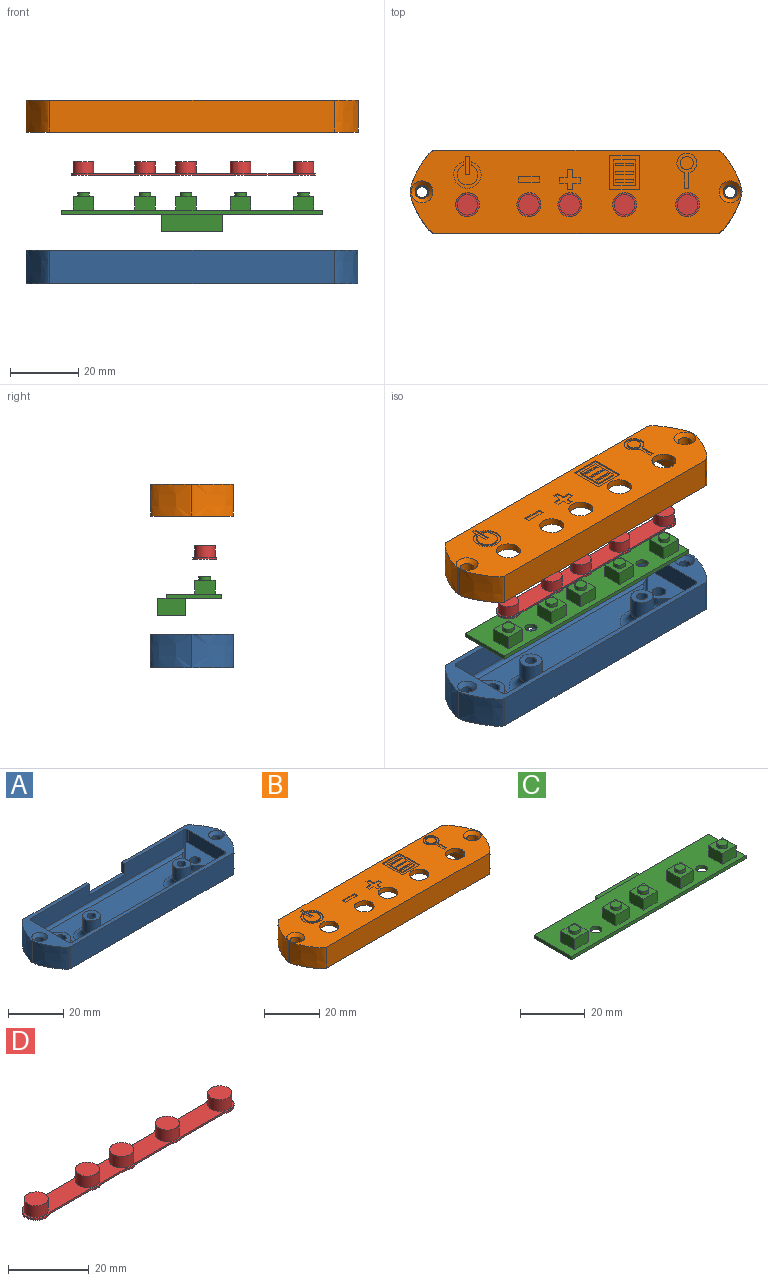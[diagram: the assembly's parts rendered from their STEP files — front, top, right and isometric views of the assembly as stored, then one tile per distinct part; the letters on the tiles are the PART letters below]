
ASSEMBLY  parts=4 mates=3
PART A: 54 faces, bbox 97.2x24.2x9.7 mm
  f0: cylinder r=2mm len=4mm, axis (0,0,1), area 50.3mm2, adj f12,f35
  f1: cylinder r=2mm len=4mm, axis (0,0,1), area 50.3mm2, adj f12,f33
  f2: plane 97.15x24.2mm, normal (0,0,1), area 457.5mm2, adj f3,f4,f5,f6,f7,f8,f11,f16
  f3: plane 77.75x7.8mm, normal (0,-1,0), area 520.1mm2, adj f2,f21,f22,f23,f37,f39,f40
  f4: extruded ~12.1x9.7mm, area 139.3mm2, adj f2,f5,f11,f12
  f5: plane 83.15x9.7mm, normal (0,1,0), area 720.2mm2, adj f2,f4,f6,f12,f21,f22,f23
  f6: extruded ~12.1x9.7mm, area 139.3mm2, adj f2,f5,f7,f12
  f7: extruded ~12.1x9.7mm, area 139.3mm2, adj f2,f6,f8,f12
  f8: plane 83.15x9.7mm, normal (0,-1,0), area 806.6mm2, adj f2,f7,f11,f12
  f9: cylinder r=1.6mm len=8.5mm, axis (0,0,1), area 85.5mm2, adj f12,f53
  f10: cylinder r=1.6mm len=8.5mm, axis (0,0,1), area 85.5mm2, adj f12,f52
  f11: extruded ~12.1x9.7mm, area 139.3mm2, adj f2,f4,f8,f12
  f12: plane 97.15x24.2mm, normal (0,0,-1), area 2190.5mm2, adj f0,f1,f4,f5,f6,f7,f8,f9
  f13: plane 7.83x7.77mm, normal (0.7,0.71,0), area 23.2mm2, adj f14,f33,f36,f37
  f14: cylinder r=3.5mm len=4.97mm, axis (0,0,1), area 11.6mm2, adj f13,f15,f33,f38
  f15: plane 7.83x7.77mm, normal (0.7,-0.71,0), area 23.2mm2, adj f14,f33,f41,f42
  f16: plane 77.75x7.8mm, normal (0,1,0), area 606.5mm2, adj f2,f41,f44,f45
  f17: plane 7.83x7.77mm, normal (-0.7,-0.71,0), area 23.2mm2, adj f18,f35,f44,f47
  f18: cylinder r=3.5mm len=4.97mm, axis (0,0,1), area 11.6mm2, adj f17,f19,f35,f46
  f19: plane 7.83x7.77mm, normal (-0.7,0.71,0), area 23.2mm2, adj f18,f35,f40,f43
  f20: plane 74.32x18.8mm, normal (0,0,1), area 979.2mm2, adj f36,f38,f39,f42,f43,f45,f46,f47
  f21: plane 4.8x1.5mm, normal (-1,0,0), area 7.2mm2, adj f2,f3,f5,f23
  f22: plane 4.8x1.5mm, normal (1,0,0), area 7.2mm2, adj f2,f3,f5,f23
  f23: plane 18x1.5mm, normal (0,0,1), area 27mm2, adj f3,f5,f21,f22
  f24: cylinder r=1.6mm len=9mm, axis (0,0,1), area 90.5mm2, adj f26,f27
  f25: cylinder r=3.25mm len=6.5mm, axis (0,0,1), area 119.7mm2, adj f26,f50,f51
  f26: plane 6.5x6.5mm, normal (0,0,1), area 25.1mm2, adj f24,f25
  f27: plane 3.2x3.2mm, normal (0,0,1), area 8mm2, adj f24
  f28: cylinder r=1.6mm len=9mm, axis (0,0,1), area 90.5mm2, adj f30,f31
  f29: cylinder r=3.25mm len=6.5mm, axis (0,0,1), area 119.7mm2, adj f30,f48,f49
  f30: plane 6.5x6.5mm, normal (0,0,1), area 25.1mm2, adj f28,f29
  f31: plane 3.2x3.2mm, normal (0,0,1), area 8mm2, adj f28
  f32: plane 18.8x5.7mm, normal (1,0,0), area 107.2mm2, adj f2,f33,f37,f41
  f33: plane 20.5x9.22mm, normal (0,0,1), area 97.7mm2, adj f1,f13,f14,f15,f32,f37,f41
  f34: plane 18.8x5.7mm, normal (-1,0,0), area 107.2mm2, adj f2,f35,f40,f44
  f35: plane 20.5x9.22mm, normal (0,0,1), area 97.7mm2, adj f0,f17,f18,f19,f34,f40,f44
  f36: cylinder r=1.2mm len=8.67mm, axis (0.71,-0.7,0), area 19.4mm2, adj f13,f20,f37,f38,f39
  f37: cylinder r=1.2mm len=8.48mm, axis (0,0,1), area 13mm2, adj f2,f3,f13,f32,f33,f36,f39
  f38: torus R=4.7mm, axis (0,0,1), area 11.7mm2, adj f14,f20,f36,f42
  f39: cylinder r=1.2mm len=79.12mm, axis (-1,0,0), area 145.9mm2, adj f3,f20,f36,f37,f40,f43
  f40: cylinder r=1.2mm len=8.48mm, axis (0,0,-1), area 13mm2, adj f2,f3,f19,f34,f35,f39,f43
  f41: cylinder r=1.2mm len=8.48mm, axis (0,0,-1), area 13mm2, adj f2,f15,f16,f32,f33,f42,f45
  f42: cylinder r=1.2mm len=8.67mm, axis (-0.71,-0.7,0), area 19.4mm2, adj f15,f20,f38,f41,f45
  f43: cylinder r=1.2mm len=8.67mm, axis (0.71,0.7,0), area 19.4mm2, adj f19,f20,f39,f40,f46
  f44: cylinder r=1.2mm len=8.48mm, axis (0,0,1), area 13mm2, adj f2,f16,f17,f34,f35,f45,f47
  f45: cylinder r=1.2mm len=79.12mm, axis (1,0,0), area 145.9mm2, adj f16,f20,f41,f42,f44,f47,f49,f51
  f46: torus R=4.7mm, axis (0,0,1), area 11.7mm2, adj f18,f20,f43,f47
  f47: cylinder r=1.2mm len=8.67mm, axis (-0.71,0.7,0), area 19.4mm2, adj f17,f20,f44,f45,f46
  f48: torus R=6.39mm, axis (0,0,1), area 113.9mm2, adj f20,f29,f49
  f49: bspline ~7.56x3.55mm, area 18.6mm2, adj f29,f45,f48
  f50: torus R=6.39mm, axis (0,0,1), area 113.9mm2, adj f20,f25,f51
  f51: bspline ~7.56x3.55mm, area 18.6mm2, adj f25,f45,f50
  f52: cone r=1.6mm half-angle=45deg, axis (0,0,1), area 23.5mm2, adj f2,f10
  f53: cone r=2.8mm half-angle=45deg, axis (0,0,1), area 23.5mm2, adj f2,f9
PART B: 94 faces, bbox 97.2x24.2x9.3 mm
  f0: plane 97.15x24.2mm, normal (0,0,1), area 1803.1mm2, adj f2,f3,f4,f5,f6,f8,f10,f11
  f1: plane 97.15x24.2mm, normal (0,0,-1), area 508.6mm2, adj f2,f3,f4,f5,f6,f7,f8,f9
  f2: plane 83.15x9.25mm, normal (0,-1,0), area 769.1mm2, adj f0,f1,f3,f8
  f3: extruded ~12.1x9.25mm, area 132.8mm2, adj f0,f1,f2,f4
  f4: extruded ~12.1x9.25mm, area 132.8mm2, adj f0,f1,f3,f5
  f5: plane 83.15x9.25mm, normal (0,1,0), area 769.1mm2, adj f0,f1,f4,f6
  f6: extruded ~12.1x9.25mm, area 132.8mm2, adj f0,f1,f5,f8
  f7: cylinder r=2mm len=8.05mm, axis (0,0,-1), area 101.2mm2, adj f1,f92
  f8: extruded ~12.1x9.25mm, area 132.8mm2, adj f0,f1,f2,f6
  f9: cylinder r=2mm len=8.05mm, axis (0,0,-1), area 101.2mm2, adj f1,f93
  f10: cylinder r=3.5mm len=7mm, axis (0,0,-1), area 44mm2, adj f0,f15
  f11: cylinder r=3.5mm len=7mm, axis (0,0,-1), area 44mm2, adj f0,f15
  f12: cylinder r=3.5mm len=7mm, axis (0,0,-1), area 44mm2, adj f0,f15
  f13: cylinder r=3.5mm len=7mm, axis (0,0,-1), area 44mm2, adj f0,f15
  f14: cylinder r=3.5mm len=7mm, axis (0,0,-1), area 44mm2, adj f0,f15
  f15: plane 77.75x18.8mm, normal (0,0,-1), area 1269.3mm2, adj f10,f11,f12,f13,f14,f83,f84,f88
  f16: plane 77.75x6.05mm, normal (0,1,0), area 470.4mm2, adj f1,f80,f84,f85
  f17: plane 18.8x6.05mm, normal (1,0,0), area 113.7mm2, adj f1,f80,f82,f83
  f18: plane 77.75x6.05mm, normal (0,-1,0), area 470.4mm2, adj f1,f82,f88,f91
  f19: plane 18.8x6.05mm, normal (-1,0,0), area 113.7mm2, adj f1,f85,f89,f91
  f20: plane 1.6x0.4mm, normal (-1,0,0), area 0.6mm2, adj f0,f21,f23,f24
  f21: plane 6x0.4mm, normal (0,-1,0), area 2.4mm2, adj f0,f20,f22,f24
  f22: plane 1.6x0.4mm, normal (1,0,0), area 0.6mm2, adj f0,f21,f23,f24
  f23: plane 6x0.4mm, normal (0,1,0), area 2.4mm2, adj f0,f20,f22,f24
  f24: plane 6x1.6mm, normal (0,0,1), area 9.6mm2, adj f20,f21,f22,f23
  f25: plane 4.53x0.4mm, normal (-1,0,0), area 1.8mm2, adj f0,f26,f28,f30
  f26: cylinder r=2.9mm len=5.8mm, axis (0,0,1), area 6.8mm2, adj f0,f25,f27,f30
  f27: plane 4.53x0.4mm, normal (1,0,0), area 1.8mm2, adj f0,f26,f28,f30
  f28: plane 1.2x0.4mm, normal (0,1,0), area 0.5mm2, adj f0,f25,f27,f30
  f29: cylinder r=1.9mm len=3.8mm, axis (0,0,1), area 4.8mm2, adj f30,f63
  f30: plane 10.27x5.8mm, normal (0,0,1), area 20.5mm2, adj f25,f26,f27,f28,f29
  f31: plane 8.76x0.4mm, normal (0,1,0), area 3.5mm2, adj f0,f32,f38,f39
  f32: plane 10x0.4mm, normal (-1,0,0), area 4mm2, adj f0,f31,f33,f39
  f33: plane 8.76x0.4mm, normal (0,-1,0), area 3.5mm2, adj f0,f32,f38,f39
  f34: plane 7.6x0.4mm, normal (-1,0,0), area 3mm2, adj f35,f37,f39,f64
  f35: plane 6.36x0.4mm, normal (0,1,0), area 2.5mm2, adj f34,f36,f39,f64
  f36: plane 7.6x0.4mm, normal (1,0,0), area 3mm2, adj f35,f37,f39,f64
  f37: plane 6.36x0.4mm, normal (0,-1,0), area 2.5mm2, adj f34,f36,f39,f64
  f38: plane 10x0.4mm, normal (1,0,0), area 4mm2, adj f0,f31,f33,f39
  f39: plane 10x8.76mm, normal (0,0,1), area 39.3mm2, adj f31,f32,f33,f34,f35,f36,f37,f38
  f40: plane 1.94x0.4mm, normal (-1,0,0), area 0.8mm2, adj f0,f41,f51,f52
  f41: plane 2.2x0.4mm, normal (0,1,0), area 0.9mm2, adj f0,f40,f42,f52
  f42: plane 1.6x0.4mm, normal (-1,0,0), area 0.6mm2, adj f0,f41,f43,f52
  f43: plane 2.2x0.4mm, normal (0,-1,0), area 0.9mm2, adj f0,f42,f44,f52
  f44: plane 2.46x0.4mm, normal (-1,0,0), area 1mm2, adj f0,f43,f45,f52
  f45: plane 1.6x0.4mm, normal (0,-1,0), area 0.6mm2, adj f0,f44,f46,f52
  f46: plane 2.46x0.4mm, normal (1,0,0), area 1mm2, adj f0,f45,f47,f52
  f47: plane 2.2x0.4mm, normal (0,-1,0), area 0.9mm2, adj f0,f46,f48,f52
  f48: plane 1.6x0.4mm, normal (1,0,0), area 0.6mm2, adj f0,f47,f49,f52
  f49: plane 2.2x0.4mm, normal (0,1,0), area 0.9mm2, adj f0,f48,f50,f52
  f50: plane 1.94x0.4mm, normal (1,0,0), area 0.8mm2, adj f0,f49,f51,f52
  f51: plane 1.6x0.4mm, normal (0,1,0), area 0.6mm2, adj f0,f40,f50,f52
  f52: plane 6x6mm, normal (0,0,1), area 16.6mm2, adj f40,f41,f42,f43,f44,f45,f46,f47
  f53: plane 1.2x0.4mm, normal (0,1,0), area 0.5mm2, adj f0,f54,f56,f57
  f54: plane 5.45x0.4mm, normal (-1,0,0), area 2.2mm2, adj f0,f53,f55,f57
  f55: plane 1.2x0.4mm, normal (0,-1,0), area 0.5mm2, adj f0,f54,f56,f57
  f56: plane 5.45x0.4mm, normal (1,0,0), area 2.2mm2, adj f0,f53,f55,f57
  f57: plane 5.45x1.2mm, normal (0,0,1), area 6.5mm2, adj f53,f54,f55,f56
  f58: plane 1.06x0.4mm, normal (1,0,0), area 0.4mm2, adj f0,f59,f61,f62
  f59: cylinder r=3mm len=6mm, axis (0,0,1), area 6.6mm2, adj f0,f58,f60,f62
  f60: plane 1.06x0.4mm, normal (-1,0,0), area 0.4mm2, adj f0,f59,f61,f62
  f61: cylinder r=4mm len=8mm, axis (0,0,1), area 9.1mm2, adj f0,f58,f60,f62
  f62: plane 8x7.83mm, normal (0,0,1), area 19.6mm2, adj f58,f59,f60,f61
  f63: plane 3.8x3.8mm, normal (0,0,1), area 11.3mm2, adj f29
  f64: plane 7.6x6.36mm, normal (0,0,1), area 36.1mm2, adj f34,f35,f36,f37,f65,f66,f67,f68
  f65: plane 0.8x0.4mm, normal (1,0,0), area 0.3mm2, adj f64,f66,f68,f69
  f66: plane 5.11x0.4mm, normal (0,1,0), area 2mm2, adj f64,f65,f67,f69
  f67: plane 0.8x0.4mm, normal (-1,0,0), area 0.3mm2, adj f64,f66,f68,f69
  f68: plane 5.11x0.4mm, normal (0,-1,0), area 2mm2, adj f64,f65,f67,f69
  f69: plane 5.11x0.8mm, normal (0,0,1), area 4.1mm2, adj f65,f66,f67,f68
  f70: plane 0.8x0.4mm, normal (1,0,0), area 0.3mm2, adj f64,f71,f73,f74
  f71: plane 5.11x0.4mm, normal (0,1,0), area 2mm2, adj f64,f70,f72,f74
  f72: plane 0.8x0.4mm, normal (-1,0,0), area 0.3mm2, adj f64,f71,f73,f74
  f73: plane 5.11x0.4mm, normal (0,-1,0), area 2mm2, adj f64,f70,f72,f74
  f74: plane 5.11x0.8mm, normal (0,0,1), area 4.1mm2, adj f70,f71,f72,f73
  f75: plane 0.8x0.4mm, normal (1,0,0), area 0.3mm2, adj f64,f76,f78,f79
  f76: plane 5.11x0.4mm, normal (0,1,0), area 2mm2, adj f64,f75,f77,f79
  f77: plane 0.8x0.4mm, normal (-1,0,0), area 0.3mm2, adj f64,f76,f78,f79
  f78: plane 5.11x0.4mm, normal (0,-1,0), area 2mm2, adj f64,f75,f77,f79
  f79: plane 5.11x0.8mm, normal (0,0,1), area 4.1mm2, adj f75,f76,f77,f78
  f80: cylinder r=1.2mm len=6.05mm, axis (0,0,1), area 11.4mm2, adj f1,f16,f17,f81
  f81: sphere r=1.2mm, area 2.3mm2, adj f80,f83,f84
  f82: cylinder r=1.2mm len=6.05mm, axis (0,0,1), area 11.4mm2, adj f1,f17,f18,f86
  f83: cylinder r=1.2mm len=18.8mm, axis (0,-1,0), area 35.4mm2, adj f15,f17,f81,f86
  f84: cylinder r=1.2mm len=77.75mm, axis (1,0,0), area 146.6mm2, adj f15,f16,f81,f87
  f85: cylinder r=1.2mm len=6.05mm, axis (0,0,1), area 11.4mm2, adj f1,f16,f19,f87
  f86: sphere r=1.2mm, area 2.3mm2, adj f82,f83,f88
  f87: sphere r=1.2mm, area 2.3mm2, adj f84,f85,f89
  f88: cylinder r=1.2mm len=77.75mm, axis (-1,0,0), area 146.6mm2, adj f15,f18,f86,f90
  f89: cylinder r=1.2mm len=18.8mm, axis (0,1,0), area 35.4mm2, adj f15,f19,f87,f90
  f90: sphere r=1.2mm, area 2.3mm2, adj f88,f89,f91
  f91: cylinder r=1.2mm len=6.05mm, axis (0,0,1), area 11.4mm2, adj f1,f18,f19,f90
  f92: cone r=2mm half-angle=45deg, axis (0,0,1), area 27.7mm2, adj f0,f7
  f93: cone r=3.2mm half-angle=45deg, axis (0,0,1), area 27.7mm2, adj f0,f9
PART C: 49 faces, bbox 76.2x18.7x11.4 mm
  f0: plane 76.15x16.2mm, normal (0,0,-1), area 1111.2mm2, adj f1,f2,f3,f4,f6,f7,f44,f45
  f1: plane 76.15x1.2mm, normal (0,1,0), area 91.4mm2, adj f0,f2,f4,f5,f43
  f2: plane 16.2x1.2mm, normal (-1,0,0), area 19.4mm2, adj f0,f1,f3,f5
  f3: plane 76.15x1.2mm, normal (0,-1,0), area 91.4mm2, adj f0,f2,f4,f5
  f4: plane 16.2x1.2mm, normal (1,0,0), area 19.4mm2, adj f0,f1,f3,f5
  f5: plane 76.15x16.2mm, normal (0,0,1), area 1033.8mm2, adj f1,f2,f3,f4,f6,f7,f8,f9
  f6: cylinder r=1.78mm len=3.55mm, axis (0,0,-1), area 13.4mm2, adj f0,f5
  f7: cylinder r=1.78mm len=3.55mm, axis (0,0,-1), area 13.4mm2, adj f0,f5
  f8: plane 6x4.05mm, normal (-1,0,0), area 24.3mm2, adj f5,f9,f11,f12
  f9: plane 6x4.05mm, normal (0,-1,0), area 24.3mm2, adj f5,f8,f10,f12
  f10: plane 6x4.05mm, normal (1,0,0), area 24.3mm2, adj f5,f9,f11,f12
  f11: plane 6x4.05mm, normal (0,1,0), area 24.3mm2, adj f5,f8,f10,f12
  f12: plane 6x6mm, normal (0,0,1), area 26.7mm2, adj f8,f9,f10,f11,f13
  f13: cylinder r=1.72mm len=3.45mm, axis (0,0,-1), area 12.5mm2, adj f12,f14
  f14: plane 3.45x3.45mm, normal (0,0,1), area 9.3mm2, adj f13
  f15: plane 6x4.05mm, normal (0,-1,0), area 24.3mm2, adj f5,f16,f18,f19
  f16: plane 6x4.05mm, normal (1,0,0), area 24.3mm2, adj f5,f15,f17,f19
  f17: plane 6x4.05mm, normal (0,1,0), area 24.3mm2, adj f5,f16,f18,f19
  f18: plane 6x4.05mm, normal (-1,0,0), area 24.3mm2, adj f5,f15,f17,f19
  f19: plane 6x6mm, normal (0,0,1), area 26.7mm2, adj f15,f16,f17,f18,f20
  f20: cylinder r=1.72mm len=3.45mm, axis (0,0,-1), area 12.5mm2, adj f19,f21
  f21: plane 3.45x3.45mm, normal (0,0,1), area 9.3mm2, adj f20
  f22: plane 6x4.05mm, normal (0,-1,0), area 24.3mm2, adj f5,f23,f25,f26
  f23: plane 6x4.05mm, normal (1,0,0), area 24.3mm2, adj f5,f22,f24,f26
  f24: plane 6x4.05mm, normal (0,1,0), area 24.3mm2, adj f5,f23,f25,f26
  f25: plane 6x4.05mm, normal (-1,0,0), area 24.3mm2, adj f5,f22,f24,f26
  f26: plane 6x6mm, normal (0,0,1), area 26.7mm2, adj f22,f23,f24,f25,f27
  f27: cylinder r=1.72mm len=3.45mm, axis (0,0,-1), area 12.5mm2, adj f26,f28
  f28: plane 3.45x3.45mm, normal (0,0,1), area 9.3mm2, adj f27
  f29: plane 6x4.05mm, normal (0,-1,0), area 24.3mm2, adj f5,f30,f32,f33
  f30: plane 6x4.05mm, normal (1,0,0), area 24.3mm2, adj f5,f29,f31,f33
  f31: plane 6x4.05mm, normal (0,1,0), area 24.3mm2, adj f5,f30,f32,f33
  f32: plane 6x4.05mm, normal (-1,0,0), area 24.3mm2, adj f5,f29,f31,f33
  f33: plane 6x6mm, normal (0,0,1), area 26.7mm2, adj f29,f30,f31,f32,f34
  f34: cylinder r=1.72mm len=3.45mm, axis (0,0,-1), area 12.5mm2, adj f33,f35
  f35: plane 3.45x3.45mm, normal (0,0,1), area 9.3mm2, adj f34
  f36: plane 6x4.05mm, normal (0,-1,0), area 24.3mm2, adj f5,f37,f39,f40
  f37: plane 6x4.05mm, normal (1,0,0), area 24.3mm2, adj f5,f36,f38,f40
  f38: plane 6x4.05mm, normal (0,1,0), area 24.3mm2, adj f5,f37,f39,f40
  f39: plane 6x4.05mm, normal (-1,0,0), area 24.3mm2, adj f5,f36,f38,f40
  f40: plane 6x6mm, normal (0,0,1), area 26.7mm2, adj f36,f37,f38,f39,f41
  f41: cylinder r=1.72mm len=3.45mm, axis (0,0,-1), area 12.5mm2, adj f40,f42
  f42: plane 3.45x3.45mm, normal (0,0,1), area 9.3mm2, adj f41
  f43: plane 18x2.5mm, normal (0,0,1), area 45mm2, adj f1,f44,f46,f47
  f44: plane 8.2x5mm, normal (-1,0,0), area 41mm2, adj f0,f43,f45,f47,f48
  f45: plane 18x5mm, normal (0,-1,0), area 90mm2, adj f0,f44,f46,f48
  f46: plane 8.2x5mm, normal (1,0,0), area 41mm2, adj f0,f43,f45,f47,f48
  f47: plane 18x5mm, normal (0,1,0), area 90mm2, adj f43,f44,f46,f48
  f48: plane 18x8.2mm, normal (0,0,-1), area 147.6mm2, adj f44,f45,f46,f47
PART D: 28 faces, bbox 71.4x7x4 mm
  f0: plane 14.39x0.5mm, normal (0,1,0), area 7.2mm2, adj f1,f15,f16,f17
  f1: cylinder r=3.5mm len=7mm, axis (0,0,-1), area 7.4mm2, adj f0,f2,f16,f17
  f2: plane 14.39x0.5mm, normal (0,-1,0), area 7.2mm2, adj f1,f3,f16,f17
  f3: cylinder r=3.5mm len=3.61mm, axis (0,0,-1), area 1.9mm2, adj f2,f4,f16,f17
  f4: plane 8.39x0.5mm, normal (0,-1,0), area 4.2mm2, adj f3,f5,f16,f17
  f5: cylinder r=3.5mm len=3.61mm, axis (0,0,-1), area 1.9mm2, adj f4,f6,f16,f17
  f6: plane 12.39x0.5mm, normal (0,-1,0), area 6.2mm2, adj f5,f7,f16,f17
  f7: cylinder r=3.5mm len=3.61mm, axis (0,0,-1), area 1.9mm2, adj f6,f8,f16,f17
  f8: plane 14.79x0.5mm, normal (0,-1,0), area 7.4mm2, adj f7,f9,f16,f17
  f9: cylinder r=3.5mm len=7mm, axis (0,0,-1), area 7.4mm2, adj f8,f10,f16,f17
  f10: plane 14.79x0.5mm, normal (0,1,0), area 7.4mm2, adj f9,f11,f16,f17
  f11: cylinder r=3.5mm len=3.61mm, axis (0,0,-1), area 1.9mm2, adj f10,f12,f16,f17
  f12: plane 12.39x0.5mm, normal (0,1,0), area 6.2mm2, adj f11,f13,f16,f17
  f13: cylinder r=3.5mm len=3.61mm, axis (0,0,-1), area 1.9mm2, adj f12,f14,f16,f17
  f14: plane 8.39x0.5mm, normal (0,1,0), area 4.2mm2, adj f13,f15,f16,f17
  f15: cylinder r=3.5mm len=3.61mm, axis (0,0,-1), area 1.9mm2, adj f0,f14,f16,f17
  f16: plane 71.39x7mm, normal (0,0,1), area 293.2mm2, adj f0,f1,f2,f3,f4,f5,f6,f7
  f17: plane 71.39x7mm, normal (0,0,-1), area 434.6mm2, adj f0,f1,f2,f3,f4,f5,f6,f7
  f18: cylinder r=3mm len=6mm, axis (0,0,-1), area 66mm2, adj f16,f19
  f19: plane 6x6mm, normal (0,0,1), area 28.3mm2, adj f18
  f20: cylinder r=3mm len=6mm, axis (0,0,-1), area 66mm2, adj f16,f21
  f21: plane 6x6mm, normal (0,0,1), area 28.3mm2, adj f20
  f22: cylinder r=3mm len=6mm, axis (0,0,-1), area 66mm2, adj f16,f23
  f23: plane 6x6mm, normal (0,0,1), area 28.3mm2, adj f22
  f24: cylinder r=3mm len=6mm, axis (0,0,-1), area 66mm2, adj f16,f25
  f25: plane 6x6mm, normal (0,0,1), area 28.3mm2, adj f24
  f26: cylinder r=3mm len=6mm, axis (0,0,-1), area 66mm2, adj f16,f27
  f27: plane 6x6mm, normal (0,0,1), area 28.3mm2, adj f26
PLACE A t=(4.21,-18.7,-29.56)mm
PLACE B t=(4.21,-18.7,5.07)mm
PLACE C t=(4.21,-18.7,-19)mm fixed
PLACE D t=(4.21,-18.7,-14.25)mm
MATE slider D.f9 <-> C.f41  axis (0,0,-1) through (36.83,-21.95,-7.6)mm
MATE slider C.f6 <-> A.f28  axis (0,0,-1) through (27.71,-22.02,-19)mm
MATE slider A.f10 <-> B.f7  axis (0,0,1) through (49.28,-18.2,-29.56)mm
